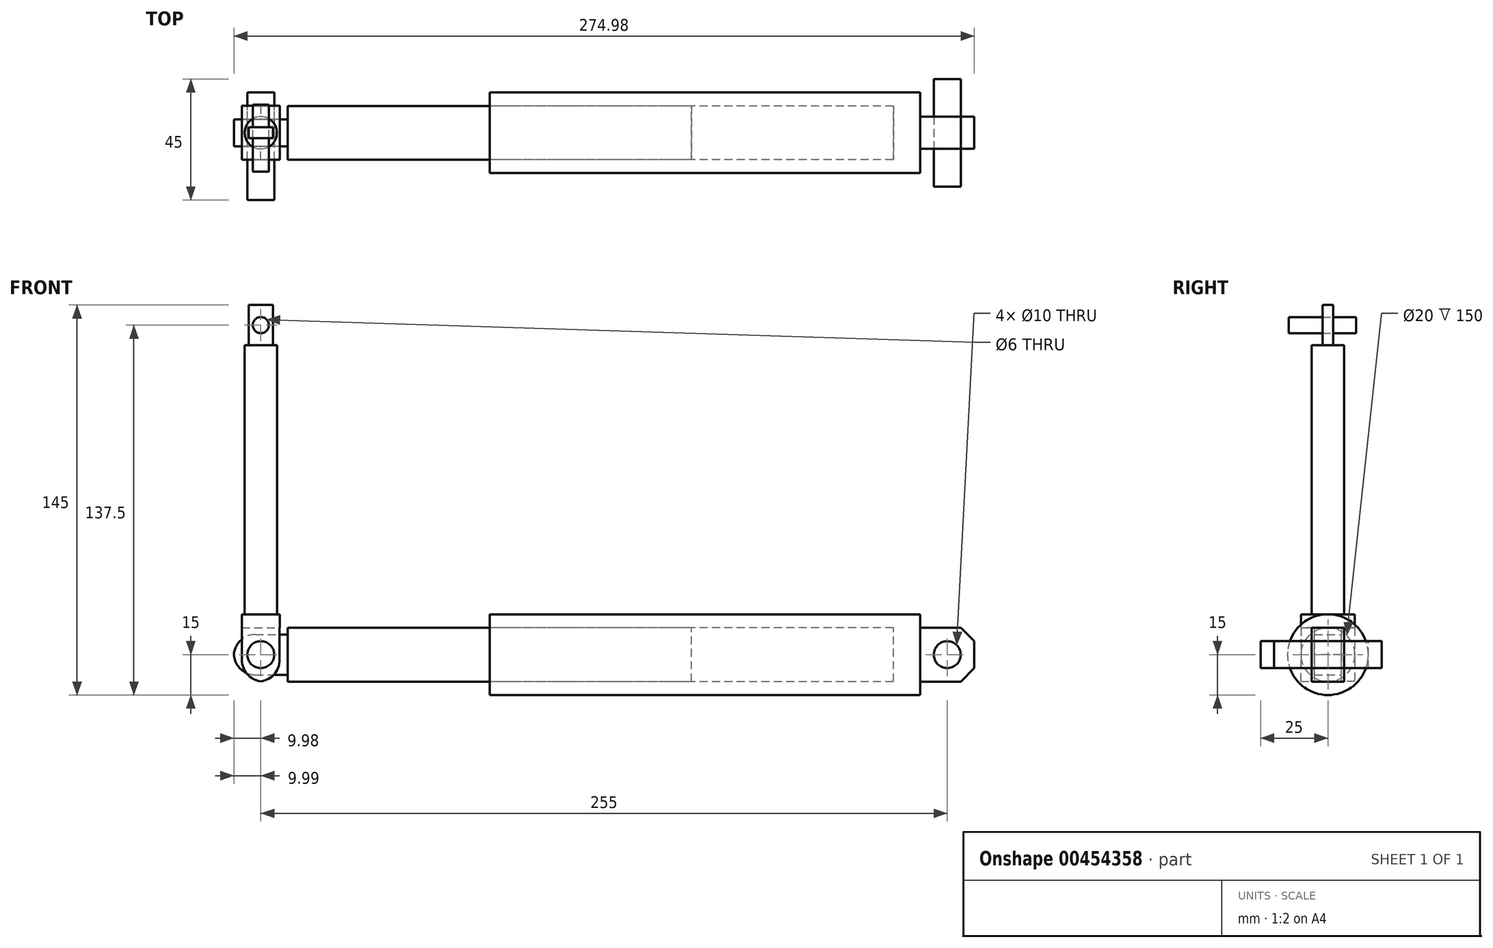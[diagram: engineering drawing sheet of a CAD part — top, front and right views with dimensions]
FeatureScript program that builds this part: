
annotation { "Feature Type Name" : "Feature", "Feature Type Description" : "" }
export const myFeature = defineFeature(function(context is Context, id is Id, definition is map)
    precondition{}
    {
        {
            var Q0;
            Q0=qCreatedBy(makeId("Right.planeOp"),FACE);
            var sketch = newSketch(context, id + "F0", { "sketchPlane" : qUnion([Q0])});
            skCircle(sketch, "E0", {"center": v(0, 0) * mm, "radius": 10 * mm});
            skSolve(sketch);
        }
        {
            var Q0;
            Q0=makeQuery(id+"F0.imprint","IMPRINT",FACE,{"disambiguationData":[TD([[makeQuery(id+"F0.imprint","IMPRINT",EDGE,{"derivedFrom":sQuery(id+"F0.wireOp",EDGE,"E0")}),1.0]])]});
            extrude(context, id + "F1", {"entities" : qUnion([Q0]), "endBound" : BoundingType.SYMMETRIC, "depth" : 150 * mm});
        }
        {
            var Q0;
            Q0=qCreatedBy(makeId("Right.planeOp"),FACE);
            var sketch = newSketch(context, id + "F2", { "sketchPlane" : qUnion([Q0])});
            skCircle(sketch, "E1.0", {"center": v(0, 0) * mm, "radius": 10 * mm});
            skCircle(sketch, "E2", {"center": v(0, 0) * mm, "radius": 15 * mm});
            skSolve(sketch);
        }
        {
            var Q0;
            Q0=makeQuery(id+"F2.imprint","IMPRINT",FACE,{"disambiguationData":[TD([[makeQuery(id+"F2.imprint","IMPRINT",EDGE,{"derivedFrom":sQuery(id+"F2.wireOp",EDGE,"E1.0")}),-1.0]])]});
            extrude(context, id + "F3", {"entities" : qUnion([Q0]), "depth" : 150 * mm});
        }
        {
            var Q0;
            Q0=makeQuery(id+"F3.opExtrude","CAP_FACE",FACE,{"disambiguationData":[OSD([sQuery(id+"F2.wireOp",EDGE,"E1.0"),sQuery(id+"F2.wireOp",EDGE,"E2")])],"isStart":false});
            var sketch = newSketch(context, id + "F4", { "sketchPlane" : qUnion([Q0])});
            skCircle(sketch, "E3.0", {"center": v(0, 0) * mm, "radius": 15 * mm});
            skSolve(sketch);
        }
        {
            var Q0;
            Q0 = qSketchRegion(id + "F4", true);
            extrude(context, id + "F5", {"entities" : qUnion([Q0]), "operationType" : NewBodyOperationType.ADD, "depth" : 10 * mm});
        }
        {
            var Q0;
            Q0=makeQuery(id+"F5.opExtrude","CAP_FACE",FACE,{"disambiguationData":[OSD([sQuery(id+"F4.wireOp",EDGE,"E3.0")])],"isStart":false});
            var sketch = newSketch(context, id + "F6", { "sketchPlane" : qUnion([Q0])});
            skLineSegment(sketch, "E4.bottom", {"start": v(-6, 10) * mm, "end": v(6, 10) * mm});
            skLineSegment(sketch, "E4.top", {"start": v(-6, -10) * mm, "end": v(6, -10) * mm});
            skLineSegment(sketch, "E4.left", {"start": v(-6, 10) * mm, "end": v(-6, -10) * mm});
            skLineSegment(sketch, "E4.right", {"start": v(6, 10) * mm, "end": v(6, -10) * mm});
            skSolve(sketch);
        }
        {
            var Q0;
            Q0=makeQuery(id+"F6.imprint","IMPRINT",FACE,{"disambiguationData":[TD([[makeQuery(id+"F6.imprint","IMPRINT",EDGE,{"derivedFrom":sQuery(id+"F6.wireOp",EDGE,"E4.bottom")}),-1.0]])]});
            extrude(context, id + "F7", {"entities" : qUnion([Q0]), "operationType" : NewBodyOperationType.ADD, "depth" : 20 * mm});
        }
        {
            var Q0;
            Q0=makeQuery(id+"F7.opExtrude","SWEPT_FACE",FACE,{"disambiguationData":[OSD([sQuery(id+"F6.wireOp",EDGE,"E4.left")])]});
            var sketch = newSketch(context, id + "F8", { "sketchPlane" : qUnion([Q0])});
            skLineSegment(sketch, "E5", {"start": v(170, 10) * mm, "end": v(170, -10) * mm, "construction": true});
            skLineSegment(sketch, "E6", {"start": v(180, 0) * mm, "end": v(160, 0) * mm, "construction": true});
            skCircle(sketch, "E7", {"center": v(170, 0) * mm, "radius": 5 * mm});
            skSolve(sketch);
        }
        {
            var Q0;
            Q0=makeQuery(id+"F8.imprint","IMPRINT",FACE,{"disambiguationData":[TD([[makeQuery(id+"F8.imprint","IMPRINT",EDGE,{"derivedFrom":sQuery(id+"F8.wireOp",EDGE,"E7")}),1.0]])]});
            extrude(context, id + "F9", {"entities" : qUnion([Q0]), "operationType" : NewBodyOperationType.REMOVE, "endBound" : BoundingType.THROUGH_ALL, "oppositeDirection" : true, "depth" : 25 * mm});
        }
        {
            var Q0;
            Q0=makeQuery(id+"F7.opExtrude","CAP_EDGE",EDGE,{"disambiguationData":[OSD([sQuery(id+"F6.wireOp",EDGE,"E4.bottom")])],"isStart":false});
            var Q1;
            Q1=makeQuery(id+"F7.opExtrude","CAP_EDGE",EDGE,{"disambiguationData":[OSD([sQuery(id+"F6.wireOp",EDGE,"E4.top")])],"isStart":false});
            chamfer(context, id + "F10", {"entities" : qUnion([Q0, Q1]), "width" : 5 * mm, "tangentPropagation" : true});
        }
        {
            var Q0;
            Q0=makeQuery(id+"F1.opExtrude","CAP_FACE",FACE,{"disambiguationData":[OSD([sQuery(id+"F0.wireOp",EDGE,"E0")])],"isStart":true});
            var sketch = newSketch(context, id + "F11", { "sketchPlane" : qUnion([Q0])});
            skLineSegment(sketch, "E8.bottom", {"start": v(5, -7.5) * mm, "end": v(-5, -7.5) * mm});
            skLineSegment(sketch, "E8.top", {"start": v(5, 7.5) * mm, "end": v(-5, 7.5) * mm});
            skLineSegment(sketch, "E8.left", {"start": v(5, -7.5) * mm, "end": v(5, 7.5) * mm});
            skLineSegment(sketch, "E8.right", {"start": v(-5, -7.5) * mm, "end": v(-5, 7.5) * mm});
            skPoint(sketch, "E8.middle", {"position": v(0, 0) * mm});
            skSolve(sketch);
        }
        {
            var Q0;
            Q0=makeQuery(id+"F11.imprint","IMPRINT",FACE,{"disambiguationData":[TD([[makeQuery(id+"F11.imprint","IMPRINT",EDGE,{"derivedFrom":sQuery(id+"F11.wireOp",EDGE,"E8.bottom")}),-1.0]])]});
            extrude(context, id + "F12", {"entities" : qUnion([Q0]), "operationType" : NewBodyOperationType.ADD, "depth" : 20 * mm});
        }
        {
            var Q0;
            Q0=makeQuery(id+"F12.opExtrude","SWEPT_FACE",FACE,{"disambiguationData":[OSD([sQuery(id+"F11.wireOp",EDGE,"E8.left")])]});
            var sketch = newSketch(context, id + "F13", { "sketchPlane" : qUnion([Q0])});
            skLineSegment(sketch, "E9", {"start": v(-95, 0) * mm, "end": v(-75, 0) * mm, "construction": true});
            skLineSegment(sketch, "E10", {"start": v(-75, 0) * mm, "end": v(-85, 7.5) * mm, "construction": true});
            skLineSegment(sketch, "E11", {"start": v(-85, 7.5) * mm, "end": v(-85, -7.5) * mm, "construction": true});
            skCircle(sketch, "E12", {"center": v(-85, 0) * mm, "radius": 5 * mm});
            skSolve(sketch);
        }
        {
            var Q0;
            Q0=makeQuery(id+"F13.imprint","IMPRINT",FACE,{"disambiguationData":[TD([[makeQuery(id+"F13.imprint","IMPRINT",EDGE,{"derivedFrom":sQuery(id+"F13.wireOp",EDGE,"E12")}),1.0]])]});
            extrude(context, id + "F14", {"entities" : qUnion([Q0]), "operationType" : NewBodyOperationType.REMOVE, "endBound" : BoundingType.THROUGH_ALL, "oppositeDirection" : true, "depth" : 25 * mm});
        }
        {
            var Q0;
            Q0=qCreatedBy(makeId("Front.planeOp"),FACE);
            var sketch = newSketch(context, id + "F15", { "sketchPlane" : qUnion([Q0])});
            skCircle(sketch, "E13.0", {"center": v(170, 0) * mm, "radius": 5 * mm});
            skSolve(sketch);
        }
        {
            var Q0;
            Q0 = qSketchRegion(id + "F15", true);
            extrude(context, id + "F16", {"entities" : qUnion([Q0]), "endBound" : BoundingType.SYMMETRIC, "depth" : 40 * mm});
        }
        {
            var Q0;
            Q0=qCreatedBy(makeId("Top.planeOp"),FACE);
            var sketch = newSketch(context, id + "F17", { "sketchPlane" : qUnion([Q0])});
            skLineSegment(sketch, "E14.0", {"start": v(-92, 5) * mm, "end": v(-78, 5) * mm});
            skLineSegment(sketch, "E15.0", {"start": v(-92, -5) * mm, "end": v(-78, -5) * mm});
            skLineSegment(sketch, "E16.0", {"start": v(-92, -10) * mm, "end": v(-78, -10) * mm});
            skLineSegment(sketch, "E17.0", {"start": v(-92, 10) * mm, "end": v(-78, 10) * mm});
            skLineSegment(sketch, "E18.0", {"start": v(-92, -10) * mm, "end": v(-92, -5) * mm});
            skLineSegment(sketch, "E19.0", {"start": v(-78, 10) * mm, "end": v(-78, 5) * mm});
            skPoint(sketch, "E20.orphan", {"position": v(-95, -5) * mm});
            skPoint(sketch, "E21.orphan", {"position": v(-75, 5) * mm});
            skLineSegment(sketch, "E22.trimOffspring", {"start": v(-78, -5) * mm, "end": v(-78, -10) * mm});
            skLineSegment(sketch, "E23.trimOffspring", {"start": v(-92, 5) * mm, "end": v(-92, 10) * mm});
            skPoint(sketch, "E24.orphan", {"position": v(-75, -5) * mm});
            skPoint(sketch, "E25.orphan", {"position": v(-95, 5) * mm});
            skSolve(sketch);
        }
        {
            var Q0;
            Q0 = qSketchRegion(id + "F17", true);
            extrude(context, id + "F18", {"entities" : qUnion([Q0]), "endBound" : BoundingType.SYMMETRIC, "depth" : 20 * mm});
        }
        {
            var Q0;
            Q0=makeQuery(id+"F18.opExtrude","CAP_FACE",FACE,{"disambiguationData":[OSD([sQuery(id+"F17.wireOp",EDGE,"E15.0"),sQuery(id+"F17.wireOp",EDGE,"E16.0"),sQuery(id+"F17.wireOp",EDGE,"E18.0"),sQuery(id+"F17.wireOp",EDGE,"E22.trimOffspring")])],"isStart":false});
            var sketch = newSketch(context, id + "F19", { "sketchPlane" : qUnion([Q0])});
            skLineSegment(sketch, "E26.bottom", {"start": v(-92, -10) * mm, "end": v(-77.97, -10) * mm});
            skLineSegment(sketch, "E26.top", {"start": v(-92, 10.02) * mm, "end": v(-77.97, 10.02) * mm});
            skLineSegment(sketch, "E26.left", {"start": v(-92, -10) * mm, "end": v(-92, 10.02) * mm});
            skLineSegment(sketch, "E26.right", {"start": v(-77.97, -10) * mm, "end": v(-77.97, 10.02) * mm});
            skSolve(sketch);
        }
        {
            var Q0;
            Q0 = qSketchRegion(id + "F19", true);
            extrude(context, id + "F20", {"entities" : qUnion([Q0]), "operationType" : NewBodyOperationType.ADD, "depth" : 5 * mm});
        }
        {
            var Q0;
            Q0=makeQuery(id+"F12.opExtrude","SWEPT_FACE",FACE,{"disambiguationData":[OSD([sQuery(id+"F11.wireOp",EDGE,"E8.left")])]});
            var sketch = newSketch(context, id + "F21", { "sketchPlane" : qUnion([Q0])});
            skCircle(sketch, "E27.0", {"center": v(-85, 0) * mm, "radius": 5 * mm});
            skSolve(sketch);
        }
        {
            var Q0;
            Q0 = qSketchRegion(id + "F21", true);
            extrude(context, id + "F22", {"entities" : qUnion([Q0]), "endBound" : BoundingType.SYMMETRIC, "depth" : 40 * mm});
        }
        {
            var Q0;
            Q0=makeQuery(id+"F22.opExtrude","SWEPT_BODY",BODY,{"disambiguationData":[OSD([sQuery(id+"F21.wireOp",EDGE,"E27.0")])]});
            var Q1;
            Q1=makeQuery(id+"F18.opExtrude","SWEPT_BODY",BODY,{"disambiguationData":[OSD([sQuery(id+"F17.wireOp",EDGE,"E14.0"),sQuery(id+"F17.wireOp",EDGE,"E17.0"),sQuery(id+"F17.wireOp",EDGE,"E19.0"),sQuery(id+"F17.wireOp",EDGE,"E23.trimOffspring")])]});
            booleanBodies(context, id + "F23", {"operationType" : BooleanOperationType.SUBTRACTION, "tools" : qUnion([Q0]), "targets" : qUnion([Q1]), "keepTools" : true});
        }
        {
            var Q0;
            Q0=makeQuery(id+"F18.opExtrude","CAP_EDGE",EDGE,{"disambiguationData":[OSD([sQuery(id+"F17.wireOp",EDGE,"E23.trimOffspring")])],"isStart":true});
            var Q1;
            Q1=makeQuery(id+"F18.opExtrude","CAP_EDGE",EDGE,{"disambiguationData":[OSD([sQuery(id+"F17.wireOp",EDGE,"E19.0")])],"isStart":true});
            var Q2;
            Q2=makeQuery(id+"F18.opExtrude","CAP_EDGE",EDGE,{"disambiguationData":[OSD([sQuery(id+"F17.wireOp",EDGE,"E22.trimOffspring")])],"isStart":true});
            var Q3;
            Q3=makeQuery(id+"F18.opExtrude","CAP_EDGE",EDGE,{"disambiguationData":[OSD([sQuery(id+"F17.wireOp",EDGE,"E18.0")])],"isStart":true});
            fillet(context, id + "F24", {"entities" : qUnion([Q0, Q1, Q2, Q3]), "radius" : 8 * mm, "tangentPropagation" : true, "allowEdgeOverflow" : false});
        }
        {
            var Q0;
            Q0=makeQuery(id+"F20.opExtrude","CAP_FACE",FACE,{"disambiguationData":[OSD([sQuery(id+"F19.wireOp",EDGE,"E26.bottom"),sQuery(id+"F19.wireOp",EDGE,"E26.top"),sQuery(id+"F19.wireOp",EDGE,"E26.left"),sQuery(id+"F19.wireOp",EDGE,"E26.right")])],"isStart":false});
            var sketch = newSketch(context, id + "F25", { "sketchPlane" : qUnion([Q0])});
            skLineSegment(sketch, "E28", {"start": v(-77.97, 10.02) * mm, "end": v(-92, -10) * mm, "construction": true});
            skLineSegment(sketch, "E29", {"start": v(-92, -10) * mm, "end": v(-77.97, -10) * mm, "construction": true});
            skLineSegment(sketch, "E30", {"start": v(-77.97, -10) * mm, "end": v(-92, 10.02) * mm, "construction": true});
            skCircle(sketch, "E31", {"center": v(-84.99, 0) * mm, "radius": 6 * mm});
            skSolve(sketch);
        }
        {
            var Q0;
            Q0=makeQuery(id+"F25.imprint","IMPRINT",FACE,{"disambiguationData":[TD([[makeQuery(id+"F25.imprint","IMPRINT",EDGE,{"derivedFrom":sQuery(id+"F25.wireOp",EDGE,"E31")}),1.0]])]});
            var Q1;
            Q1=sQuery(id+"F25.wireOp",EDGE,"E31");
            extrude(context, id + "F26", {"entities" : qUnion([Q0]), "operationType" : NewBodyOperationType.ADD, "surfaceEntities" : qUnion([Q1]), "depth" : 100 * mm});
        }
        {
            var Q0;
            Q0=makeQuery(id+"F26.opExtrude","CAP_FACE",FACE,{"disambiguationData":[OSD([sQuery(id+"F25.wireOp",EDGE,"E31")])],"isStart":false});
            var sketch = newSketch(context, id + "F27", { "sketchPlane" : qUnion([Q0])});
            skLineSegment(sketch, "E32.bottom", {"start": v(-89.49, -2) * mm, "end": v(-80.49, -2) * mm});
            skLineSegment(sketch, "E32.top", {"start": v(-89.49, 2) * mm, "end": v(-80.49, 2) * mm});
            skLineSegment(sketch, "E32.left", {"start": v(-89.49, -2) * mm, "end": v(-89.49, 2) * mm});
            skLineSegment(sketch, "E32.right", {"start": v(-80.49, -2) * mm, "end": v(-80.49, 2) * mm});
            skPoint(sketch, "E32.middle", {"position": v(-84.99, 0) * mm});
            skSolve(sketch);
        }
        {
            var Q0;
            Q0=makeQuery(id+"F27.imprint","IMPRINT",FACE,{"disambiguationData":[TD([[makeQuery(id+"F27.imprint","IMPRINT",EDGE,{"derivedFrom":sQuery(id+"F27.wireOp",EDGE,"E32.bottom")}),1.0]])]});
            extrude(context, id + "F28", {"entities" : qUnion([Q0]), "operationType" : NewBodyOperationType.ADD, "depth" : 15 * mm});
        }
        {
            var Q0;
            Q0=makeQuery(id+"F28.opExtrude","SWEPT_FACE",FACE,{"disambiguationData":[OSD([sQuery(id+"F27.wireOp",EDGE,"E32.bottom")])]});
            var sketch = newSketch(context, id + "F29", { "sketchPlane" : qUnion([Q0])});
            skCircle(sketch, "E33", {"center": v(-84.99, 122.5) * mm, "radius": 3 * mm});
            skPoint(sketch, "E33.centerSnap0", {"position": v(-84.99, 130) * mm});
            skPoint(sketch, "E33.centerSnap1", {"position": v(-80.49, 122.5) * mm});
            skSolve(sketch);
        }
        {
            var Q0;
            Q0=makeQuery(id+"F29.imprint","IMPRINT",FACE,{"disambiguationData":[TD([[makeQuery(id+"F29.imprint","IMPRINT",EDGE,{"derivedFrom":sQuery(id+"F29.wireOp",EDGE,"E33")}),1.0]])]});
            extrude(context, id + "F30", {"entities" : qUnion([Q0]), "endBound" : BoundingType.SYMMETRIC, "depth" : 25 * mm});
        }
        {
            var Q0;
            Q0=makeQuery(id+"F30.opExtrude","SWEPT_BODY",BODY,{"disambiguationData":[OSD([sQuery(id+"F29.wireOp",EDGE,"E33")])]});
            var Q1;
            Q1=makeQuery(id+"F18.opExtrude","SWEPT_BODY",BODY,{"disambiguationData":[OSD([sQuery(id+"F17.wireOp",EDGE,"E14.0"),sQuery(id+"F17.wireOp",EDGE,"E17.0"),sQuery(id+"F17.wireOp",EDGE,"E19.0"),sQuery(id+"F17.wireOp",EDGE,"E23.trimOffspring")])]});
            booleanBodies(context, id + "F31", {"operationType" : BooleanOperationType.SUBTRACTION, "tools" : qUnion([Q0]), "targets" : qUnion([Q1]), "keepTools" : true});
        }
        {
            var Q0;
            Q0=makeQuery(id+"F12.opExtrude","CAP_EDGE",EDGE,{"disambiguationData":[OSD([sQuery(id+"F11.wireOp",EDGE,"E8.top")])],"isStart":false});
            var Q1;
            Q1=makeQuery(id+"F12.opExtrude","CAP_EDGE",EDGE,{"disambiguationData":[OSD([sQuery(id+"F11.wireOp",EDGE,"E8.bottom")])],"isStart":false});
            fillet(context, id + "F32", {"entities" : qUnion([Q0, Q1]), "radius" : 8 * mm, "tangentPropagation" : true, "allowEdgeOverflow" : false});
        }
    });
